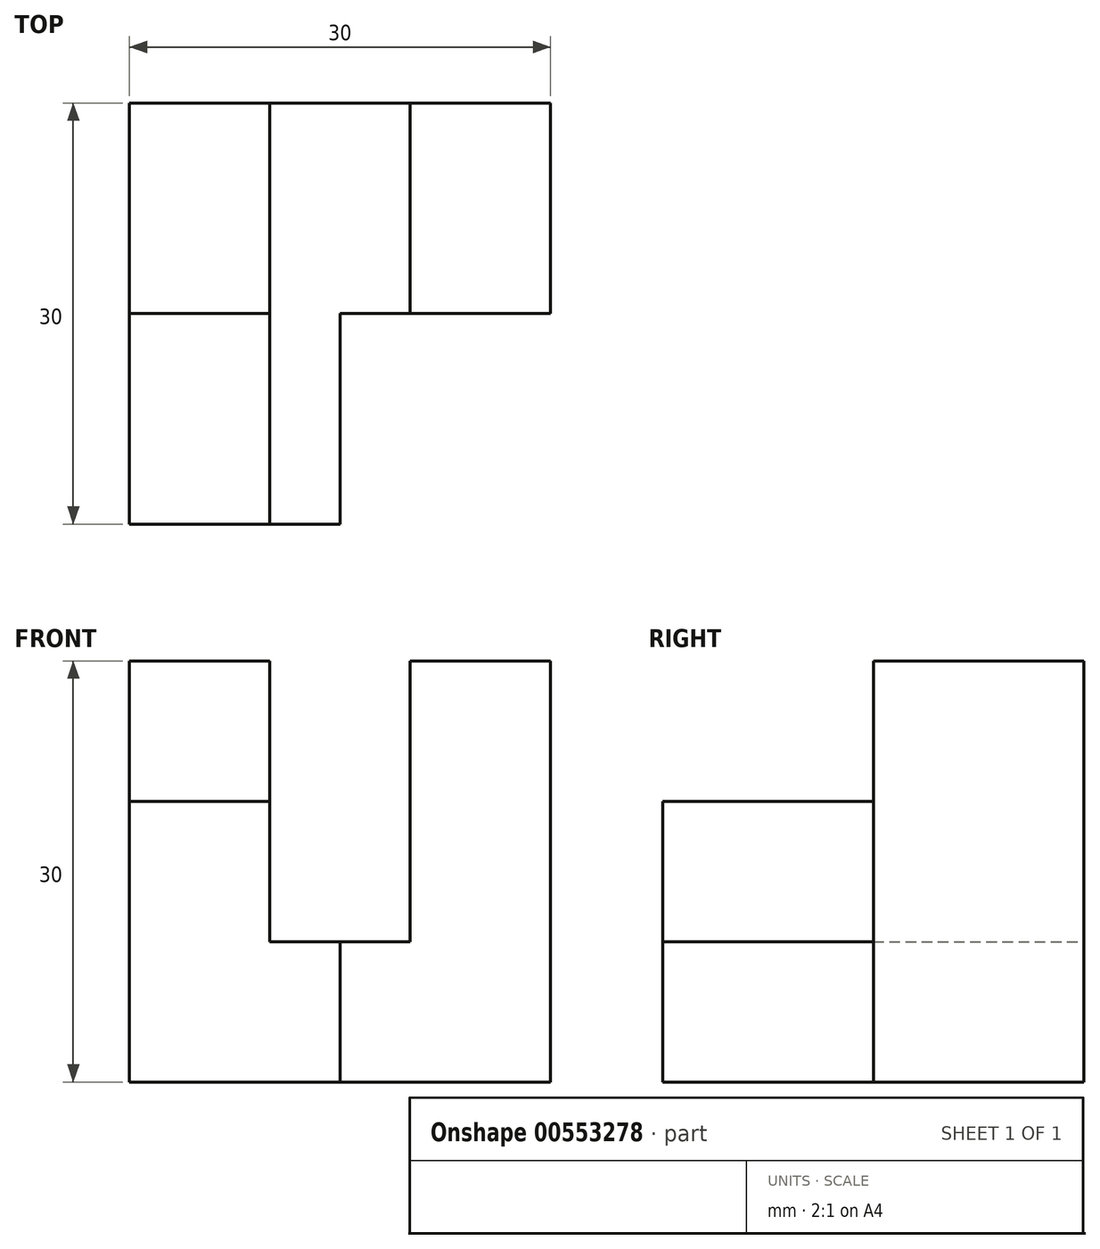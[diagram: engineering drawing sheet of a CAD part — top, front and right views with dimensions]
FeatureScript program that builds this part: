
annotation { "Feature Type Name" : "Feature", "Feature Type Description" : "" }
export const myFeature = defineFeature(function(context is Context, id is Id, definition is map)
    precondition{}
    {
        {
            var Q0;
            Q0=qCreatedBy(makeId("Top.planeOp"),FACE);
            var sketch = newSketch(context, id + "F0", { "sketchPlane" : qUnion([Q0])});
            skLineSegment(sketch, "E0.bottom", {"start": v(0, 0) * mm, "end": v(30, 0) * mm});
            skLineSegment(sketch, "E0.top", {"start": v(0, 30) * mm, "end": v(30, 30) * mm});
            skLineSegment(sketch, "E0.left", {"start": v(0, 0) * mm, "end": v(0, 30) * mm});
            skLineSegment(sketch, "E0.right", {"start": v(30, 0) * mm, "end": v(30, 30) * mm});
            skSolve(sketch);
        }
        {
            var Q0;
            Q0=qSketchRegion(id+"F0",true);
            extrude(context, id + "F1", {"entities" : qUnion([Q0]), "depth" : 30 * mm, "offsetDistance" : 25 * mm});
        }
        {
            var Q0;
            Q0=makeQuery(id+"F1.opExtrude","CAP_FACE",FACE,{"disambiguationData":[OSD([sQuery(id+"F0.wireOp",EDGE,"E0.bottom"),sQuery(id+"F0.wireOp",EDGE,"E0.top"),sQuery(id+"F0.wireOp",EDGE,"E0.left"),sQuery(id+"F0.wireOp",EDGE,"E0.right")])],"isStart":false});
            var sketch = newSketch(context, id + "F2", { "sketchPlane" : qUnion([Q0])});
            skLineSegment(sketch, "E1.bottom", {"start": v(10, 0) * mm, "end": v(20, 0) * mm});
            skLineSegment(sketch, "E1.top", {"start": v(10, 30) * mm, "end": v(20, 30) * mm});
            skLineSegment(sketch, "E1.left", {"start": v(10, 0) * mm, "end": v(10, 30) * mm});
            skLineSegment(sketch, "E1.right", {"start": v(20, 15) * mm, "end": v(20, 30) * mm});
            skLineSegment(sketch, "E2.0", {"start": v(30, 0) * mm, "end": v(30, 15) * mm});
            skLineSegment(sketch, "E3.0", {"start": v(10, 0) * mm, "end": v(30, 0) * mm});
            skLineSegment(sketch, "E4.bottom", {"start": v(30, 0) * mm, "end": v(15, 0) * mm});
            skLineSegment(sketch, "E4.top", {"start": v(30, 15) * mm, "end": v(20, 15) * mm});
            skPoint(sketch, "E5.orphan", {"position": v(30, 30) * mm});
            skPoint(sketch, "E6.orphan", {"position": v(0, 0) * mm});
            skSolve(sketch);
        }
        {
            var Q0;
            Q0 = qSketchRegion(id + "F2", true);
            extrude(context, id + "F3", {"entities" : qUnion([Q0]), "operationType" : NewBodyOperationType.REMOVE, "oppositeDirection" : true, "depth" : 20 * mm, "offsetDistance" : 25 * mm});
        }
        {
            var Q0;
            Q0=makeQuery(id+"F3.boolean.opBoolean","COPY",FACE,{"derivedFrom":makeQuery(id+"F3.opExtrude","CAP_FACE",FACE,{"disambiguationData":[OSD([sQuery(id+"F2.wireOp",EDGE,"E1.top"),sQuery(id+"F2.wireOp",EDGE,"E1.left"),sQuery(id+"F2.wireOp",EDGE,"E1.right"),sQuery(id+"F2.wireOp",EDGE,"E3.0"),sQuery(id+"F2.wireOp",EDGE,"E4.bottom"),sQuery(id+"F2.wireOp",EDGE,"E4.top"),sQuery(id+"F2.wireOp",EDGE,"E2.0")])],"isStart":false})});
            var sketch = newSketch(context, id + "F4", { "sketchPlane" : qUnion([Q0])});
            skLineSegment(sketch, "E7.bottom", {"start": v(30, 0) * mm, "end": v(15, 0) * mm});
            skLineSegment(sketch, "E7.top", {"start": v(30, 15) * mm, "end": v(15, 15) * mm});
            skLineSegment(sketch, "E7.left", {"start": v(30, 0) * mm, "end": v(30, 15) * mm});
            skLineSegment(sketch, "E7.right", {"start": v(15, 0) * mm, "end": v(15, 15) * mm});
            skSolve(sketch);
        }
        {
            var Q0;
            Q0 = qSketchRegion(id + "F4", true);
            extrude(context, id + "F5", {"entities" : qUnion([Q0]), "operationType" : NewBodyOperationType.REMOVE, "endBound" : BoundingType.THROUGH_ALL, "oppositeDirection" : true, "depth" : 1 * mm, "offsetDistance" : 25 * mm});
        }
        {
            var Q0;
            {var subQ0=sQuery(id+"F0.wireOp",EDGE,"E0.bottom");var subQ1=sQuery(id+"F0.wireOp",EDGE,"E0.top");var subQ2=sQuery(id+"F0.wireOp",EDGE,"E0.left");Q0=makeQuery(id+"F3.boolean.opBoolean","SPLIT",FACE,{"disambiguationData":[TD([makeQuery(id+"F1.opExtrude","SWEPT_FACE",FACE,{"disambiguationData":[OSD([subQ0])]})])],"derivedFrom":makeQuery(id+"F1.opExtrude","CAP_FACE",FACE,{"disambiguationData":[OSD([subQ0,subQ1,subQ2,sQuery(id+"F0.wireOp",EDGE,"E0.right")])],"isStart":false})});}
            var sketch = newSketch(context, id + "F6", { "sketchPlane" : qUnion([Q0])});
            skLineSegment(sketch, "E8.bottom", {"start": v(0, 0) * mm, "end": v(10, 0) * mm});
            skLineSegment(sketch, "E8.top", {"start": v(0, 15) * mm, "end": v(10, 15) * mm});
            skLineSegment(sketch, "E8.left", {"start": v(0, 0) * mm, "end": v(0, 15) * mm});
            skLineSegment(sketch, "E8.right", {"start": v(10, 0) * mm, "end": v(10, 15) * mm});
            skSolve(sketch);
        }
        {
            var Q0;
            Q0 = qSketchRegion(id + "F6", true);
            extrude(context, id + "F7", {"entities" : qUnion([Q0]), "operationType" : NewBodyOperationType.REMOVE, "oppositeDirection" : true, "depth" : 10 * mm, "offsetDistance" : 25 * mm});
        }
    });
